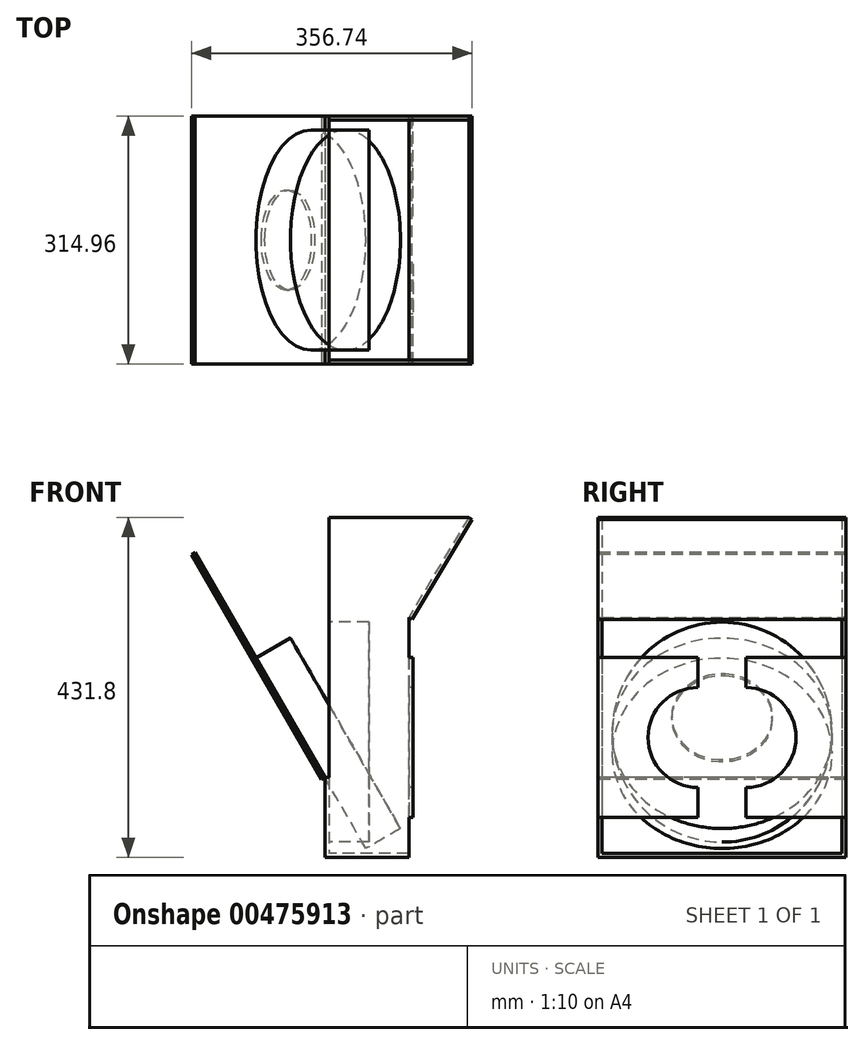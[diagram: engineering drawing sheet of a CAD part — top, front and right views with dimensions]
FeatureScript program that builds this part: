
annotation { "Feature Type Name" : "Feature", "Feature Type Description" : "" }
export const myFeature = defineFeature(function(context is Context, id is Id, definition is map)
    precondition{}
    {
        {
            var Q0;
            Q0=qCreatedBy(makeId("Top.planeOp"),FACE);
            var sketch = newSketch(context, id + "F0", { "sketchPlane" : qUnion([Q0])});
            skLineSegment(sketch, "E0.bottom", {"start": v(50.8, 152.4) * mm, "end": v(-50.8, 152.4) * mm});
            skLineSegment(sketch, "E0.top", {"start": v(50.8, -152.4) * mm, "end": v(-50.8, -152.4) * mm});
            skLineSegment(sketch, "E0.left", {"start": v(50.8, 152.4) * mm, "end": v(50.8, -152.4) * mm});
            skLineSegment(sketch, "E0.right", {"start": v(-50.8, 152.4) * mm, "end": v(-50.8, -152.4) * mm});
            skPoint(sketch, "E0.middle", {"position": v(0, 0) * mm});
            skSolve(sketch);
        }
        {
            var Q0;
            Q0=makeQuery(id+"F0.imprint","IMPRINT",FACE,{"disambiguationData":[TD([[makeQuery(id+"F0.imprint","IMPRINT",EDGE,{"derivedFrom":sQuery(id+"F0.wireOp",EDGE,"E0.bottom")}),1.0]])]});
            extrude(context, id + "F1", {"entities" : qUnion([Q0]), "endBound" : BoundingType.SYMMETRIC, "depth" : 5.08 * mm, "offsetDistance" : 25.4 * mm});
        }
        {
            var Q0;
            Q0=makeQuery(id+"F1.opExtrude","SWEPT_FACE",FACE,{"disambiguationData":[OSD([sQuery(id+"F0.wireOp",EDGE,"E0.top")])]});
            var sketch = newSketch(context, id + "F2", { "sketchPlane" : qUnion([Q0])});
            skLineSegment(sketch, "E1.bottom", {"start": v(-50.8, 429.26) * mm, "end": v(50.8, 429.26) * mm});
            skLineSegment(sketch, "E1.top", {"start": v(-50.8, -2.54) * mm, "end": v(50.8, -2.54) * mm});
            skLineSegment(sketch, "E1.left", {"start": v(-50.8, 429.26) * mm, "end": v(-50.8, -2.54) * mm});
            skLineSegment(sketch, "E1.right", {"start": v(50.8, 429.26) * mm, "end": v(50.8, -2.54) * mm});
            skLineSegment(sketch, "E2", {"start": v(50.8, 429.26) * mm, "end": v(127, 429.26) * mm});
            skLineSegment(sketch, "E3", {"start": v(127, 429.26) * mm, "end": v(50.8, 302.26) * mm});
            skSolve(sketch);
        }
        {
            var Q0;
            Q0 = qSketchRegion(id + "F2", true);
            extrude(context, id + "F3", {"entities" : qUnion([Q0]), "operationType" : NewBodyOperationType.ADD, "depth" : 5.08 * mm, "offsetDistance" : 25.4 * mm});
        }
        {
            var Q0;
            Q0=makeQuery(id+"F1.opExtrude","SWEPT_FACE",FACE,{"disambiguationData":[OSD([sQuery(id+"F0.wireOp",EDGE,"E0.bottom")])]});
            var sketch = newSketch(context, id + "F4", { "sketchPlane" : qUnion([Q0])});
            skLineSegment(sketch, "E4.bottom", {"start": v(-50.8, 429.26) * mm, "end": v(50.8, 429.26) * mm});
            skLineSegment(sketch, "E4.top", {"start": v(-50.8, -2.54) * mm, "end": v(50.8, -2.54) * mm});
            skLineSegment(sketch, "E4.left", {"start": v(-50.8, 429.26) * mm, "end": v(-50.8, -2.54) * mm});
            skLineSegment(sketch, "E4.right", {"start": v(50.8, 429.26) * mm, "end": v(50.8, -2.54) * mm});
            skLineSegment(sketch, "E5", {"start": v(-50.8, 429.26) * mm, "end": v(-127, 429.26) * mm});
            skLineSegment(sketch, "E6", {"start": v(-127, 429.26) * mm, "end": v(-50.8, 302.26) * mm});
            skSolve(sketch);
        }
        {
            var Q0;
            Q0 = qSketchRegion(id + "F4", true);
            extrude(context, id + "F5", {"entities" : qUnion([Q0]), "operationType" : NewBodyOperationType.ADD, "depth" : 5.08 * mm, "offsetDistance" : 25.4 * mm});
        }
        {
            var Q0;
            Q0=makeQuery(id+"F5.opExtrude","SWEPT_FACE",FACE,{"disambiguationData":[OSD([sQuery(id+"F4.wireOp",EDGE,"E6")])]});
            var sketch = newSketch(context, id + "F6", { "sketchPlane" : qUnion([Q0])});
            skLineSegment(sketch, "E7.bottom", {"start": v(-157.48, 285.32) * mm, "end": v(157.48, 285.32) * mm});
            skLineSegment(sketch, "E7.top", {"start": v(-157.48, 433.43) * mm, "end": v(157.48, 433.43) * mm});
            skLineSegment(sketch, "E7.left", {"start": v(-157.48, 285.32) * mm, "end": v(-157.48, 433.43) * mm});
            skLineSegment(sketch, "E7.right", {"start": v(157.48, 285.32) * mm, "end": v(157.48, 433.43) * mm});
            skSolve(sketch);
        }
        {
            var Q0;
            Q0 = qSketchRegion(id + "F6", true);
            extrude(context, id + "F7", {"entities" : qUnion([Q0]), "operationType" : NewBodyOperationType.ADD, "depth" : 5.08 * mm, "offsetDistance" : 25.4 * mm});
        }
        {
            var Q0;
            Q0=makeQuery(id+"F5.boolean.opBoolean","MERGE",FACE,{"derivedFrom":[makeQuery(id+"F3.boolean.opBoolean","MERGE",FACE,{"derivedFrom":[makeQuery(id+"F1.opExtrude","SWEPT_FACE",FACE,{"disambiguationData":[OSD([sQuery(id+"F0.wireOp",EDGE,"E0.right")])]}),makeQuery(id+"F3.opExtrude","SWEPT_FACE",FACE,{"disambiguationData":[OSD([sQuery(id+"F2.wireOp",EDGE,"E1.left")])]})]}),makeQuery(id+"F5.opExtrude","SWEPT_FACE",FACE,{"disambiguationData":[OSD([sQuery(id+"F4.wireOp",EDGE,"E4.right")])]})]});
            var sketch = newSketch(context, id + "F8", { "sketchPlane" : qUnion([Q0])});
            skLineSegment(sketch, "E8.bottom", {"start": v(-157.48, -2.54) * mm, "end": v(157.48, -2.54) * mm});
            skLineSegment(sketch, "E8.top", {"start": v(-157.48, 99.06) * mm, "end": v(157.48, 99.06) * mm});
            skLineSegment(sketch, "E8.left", {"start": v(-157.48, -2.54) * mm, "end": v(-157.48, 99.06) * mm});
            skLineSegment(sketch, "E8.right", {"start": v(157.48, -2.54) * mm, "end": v(157.48, 99.06) * mm});
            skSolve(sketch);
        }
        {
            var Q0;
            Q0 = qSketchRegion(id + "F8", true);
            extrude(context, id + "F9", {"entities" : qUnion([Q0]), "operationType" : NewBodyOperationType.ADD, "depth" : 5.08 * mm, "offsetDistance" : 25.4 * mm});
        }
        {
            var Q0;
            Q0=makeQuery(id+"F9.opExtrude","CAP_FACE",FACE,{"disambiguationData":[OSD([sQuery(id+"F8.wireOp",EDGE,"E8.bottom"),sQuery(id+"F8.wireOp",EDGE,"E8.top"),sQuery(id+"F8.wireOp",EDGE,"E8.left"),sQuery(id+"F8.wireOp",EDGE,"E8.right")])],"isStart":false});
            var sketch = newSketch(context, id + "F10", { "sketchPlane" : qUnion([Q0])});
            skLineSegment(sketch, "E9.bottom", {"start": v(-157.48, 99.06) * mm, "end": v(157.48, 99.06) * mm});
            skLineSegment(sketch, "E9.top", {"start": v(-157.48, 429.26) * mm, "end": v(157.48, 429.26) * mm});
            skLineSegment(sketch, "E9.left", {"start": v(-157.48, 99.06) * mm, "end": v(-157.48, 429.26) * mm});
            skLineSegment(sketch, "E9.right", {"start": v(157.48, 99.06) * mm, "end": v(157.48, 429.26) * mm});
            skCircle(sketch, "E10", {"center": v(0, 187.96) * mm, "radius": 63.5 * mm});
            skLineSegment(sketch, "E11", {"start": v(0, 187.96) * mm, "end": v(0, 99.06) * mm});
            skSolve(sketch);
        }
        {
            var Q0;
            Q0 = qSketchRegion(id + "F10", true);
            extrude(context, id + "F11", {"entities" : qUnion([Q0]), "depth" : 5.08 * mm, "offsetDistance" : 25.4 * mm});
        }
        {
            var Q0;
            Q0=makeQuery(id+"F11.opExtrude","SWEPT_BODY",BODY,{"disambiguationData":[OSD([sQuery(id+"F10.wireOp",EDGE,"E9.bottom"),sQuery(id+"F10.wireOp",EDGE,"E9.top"),sQuery(id+"F10.wireOp",EDGE,"E9.left"),sQuery(id+"F10.wireOp",EDGE,"E9.right")])]});
            var Q1;
            Q1=makeQuery(id+"F9.opExtrude","CAP_EDGE",EDGE,{"disambiguationData":[OSD([sQuery(id+"F8.wireOp",EDGE,"E8.top")])],"isStart":false});
            transform(context, id + "F12", {"entities" : qUnion([Q0]), "transformType" : TransformType.ROTATION, "transformAxis" : qUnion([Q1]), "angle" : 30 * degree, "makeCopy" : false});
        }
        {
            var Q0;
            Q0=makeQuery(id+"F5.boolean.opBoolean","MERGE",FACE,{"derivedFrom":[makeQuery(id+"F3.boolean.opBoolean","MERGE",FACE,{"derivedFrom":[makeQuery(id+"F1.opExtrude","SWEPT_FACE",FACE,{"disambiguationData":[OSD([sQuery(id+"F0.wireOp",EDGE,"E0.left")])]}),makeQuery(id+"F3.opExtrude","SWEPT_FACE",FACE,{"disambiguationData":[OSD([sQuery(id+"F2.wireOp",EDGE,"E1.right")])]})]}),makeQuery(id+"F5.opExtrude","SWEPT_FACE",FACE,{"disambiguationData":[OSD([sQuery(id+"F4.wireOp",EDGE,"E4.left")])]})]});
            var sketch = newSketch(context, id + "F13", { "sketchPlane" : qUnion([Q0])});
            skLineSegment(sketch, "E12.bottom", {"start": v(30.48, 48.26) * mm, "end": v(157.48, 48.26) * mm});
            skLineSegment(sketch, "E12.top", {"start": v(30.48, 251.46) * mm, "end": v(157.48, 251.46) * mm});
            skLineSegment(sketch, "E12.left", {"start": v(30.48, 48.26) * mm, "end": v(30.48, 86.36) * mm});
            skLineSegment(sketch, "E12.right", {"start": v(157.48, 48.26) * mm, "end": v(157.48, 251.46) * mm});
            skArc(sketch, "E13", {"start": v(30.48, 86.36) * mm, "mid": v(93.98, 149.86) * mm, "end": v(30.48, 213.36) * mm});
            skLineSegment(sketch, "E14.trimOffspring", {"start": v(30.48, 213.36) * mm, "end": v(30.48, 251.46) * mm});
            skSolve(sketch);
        }
        {
            var Q0;
            Q0 = qSketchRegion(id + "F13", true);
            extrude(context, id + "F14", {"entities" : qUnion([Q0]), "operationType" : NewBodyOperationType.ADD, "depth" : 5.08 * mm, "offsetDistance" : 25.4 * mm});
        }
        {
            var Q0;
            {var subQ1=sQuery(id+"F2.wireOp",EDGE,"E1.top");var subQ6=sQuery(id+"F4.wireOp",EDGE,"E4.left");var subQ11=sQuery(id+"F0.wireOp",EDGE,"E0.left");var subQ18=sQuery(id+"F2.wireOp",EDGE,"E1.right");Q0=makeQuery(id+"F14.boolean.opBoolean","SPLIT",FACE,{"disambiguationData":[TD([makeQuery(id+"F3.opExtrude","SWEPT_FACE",FACE,{"disambiguationData":[OSD([subQ1])]})])],"derivedFrom":makeQuery(id+"F5.boolean.opBoolean","MERGE",FACE,{"derivedFrom":[makeQuery(id+"F3.boolean.opBoolean","MERGE",FACE,{"derivedFrom":[makeQuery(id+"F1.opExtrude","SWEPT_FACE",FACE,{"disambiguationData":[OSD([subQ11])]}),makeQuery(id+"F3.opExtrude","SWEPT_FACE",FACE,{"disambiguationData":[OSD([subQ18])]})]}),makeQuery(id+"F5.opExtrude","SWEPT_FACE",FACE,{"disambiguationData":[OSD([subQ6])]})]})});}
            var sketch = newSketch(context, id + "F15", { "sketchPlane" : qUnion([Q0])});
            skLineSegment(sketch, "E15.bottom", {"start": v(-157.48, 251.46) * mm, "end": v(-30.48, 251.46) * mm});
            skLineSegment(sketch, "E15.top", {"start": v(-157.48, 48.26) * mm, "end": v(-30.48, 48.26) * mm});
            skLineSegment(sketch, "E15.left", {"start": v(-157.48, 251.46) * mm, "end": v(-157.48, 48.26) * mm});
            skLineSegment(sketch, "E15.right", {"start": v(-30.48, 251.46) * mm, "end": v(-30.48, 213.36) * mm});
            skArc(sketch, "E16", {"start": v(-30.48, 213.36) * mm, "mid": v(-93.98, 149.86) * mm, "end": v(-30.48, 86.36) * mm});
            skLineSegment(sketch, "E17.trimOffspring", {"start": v(-30.48, 86.36) * mm, "end": v(-30.48, 48.26) * mm});
            skSolve(sketch);
        }
        {
            var Q0;
            {var subQ0=sQuery(id+"F15.wireOp",EDGE,"E15.right");Q0=makeQuery(id+"F15.imprint","IMPRINT",FACE,{"disambiguationData":[TD([[makeQuery(id+"F15.imprint","IMPRINT",EDGE,{"derivedFrom":subQ0}),-1.0]])]});}
            var Q1;
            {var subQ0=sQuery(id+"F15.wireOp",EDGE,"E15.left");Q1=makeQuery(id+"F15.imprint","IMPRINT",FACE,{"disambiguationData":[TD([[makeQuery(id+"F15.imprint","IMPRINT",EDGE,{"derivedFrom":subQ0}),1.0]])]});}
            extrude(context, id + "F16", {"entities" : qUnion([Q0, Q1]), "operationType" : NewBodyOperationType.ADD, "depth" : 5.08 * mm, "offsetDistance" : 25.4 * mm});
        }
        {
            var Q0;
            Q0=makeQuery(id+"F9.opExtrude","CAP_FACE",FACE,{"disambiguationData":[OSD([sQuery(id+"F8.wireOp",EDGE,"E8.bottom"),sQuery(id+"F8.wireOp",EDGE,"E8.top"),sQuery(id+"F8.wireOp",EDGE,"E8.left"),sQuery(id+"F8.wireOp",EDGE,"E8.right")])],"isStart":true});
            var sketch = newSketch(context, id + "F17", { "sketchPlane" : qUnion([Q0])});
            skCircle(sketch, "E18", {"center": v(0, 156.6) * mm, "radius": 139.7 * mm});
            skSolve(sketch);
        }
        {
            var Q0;
            Q0 = qSketchRegion(id + "F17", true);
            extrude(context, id + "F18", {"entities" : qUnion([Q0]), "operationType" : NewBodyOperationType.ADD, "depth" : 50.8 * mm, "offsetDistance" : 25.4 * mm});
        }
        {
            var Q0;
            Q0=makeQuery(id+"F11.opExtrude","CAP_FACE",FACE,{"disambiguationData":[OSD([sQuery(id+"F10.wireOp",EDGE,"E9.bottom"),sQuery(id+"F10.wireOp",EDGE,"E9.top"),sQuery(id+"F10.wireOp",EDGE,"E9.left"),sQuery(id+"F10.wireOp",EDGE,"E9.right"),sQuery(id+"F10.wireOp",EDGE,"E10")])],"isStart":true});
            var sketch = newSketch(context, id + "F19", { "sketchPlane" : qUnion([Q0])});
            skCircle(sketch, "E19", {"center": v(0, 149.22) * mm, "radius": 139.7 * mm});
            skSolve(sketch);
        }
        {
            var Q0;
            Q0 = qSketchRegion(id + "F19", true);
            extrude(context, id + "F20", {"entities" : qUnion([Q0]), "depth" : 50.8 * mm, "offsetDistance" : 25.4 * mm});
        }
    });
